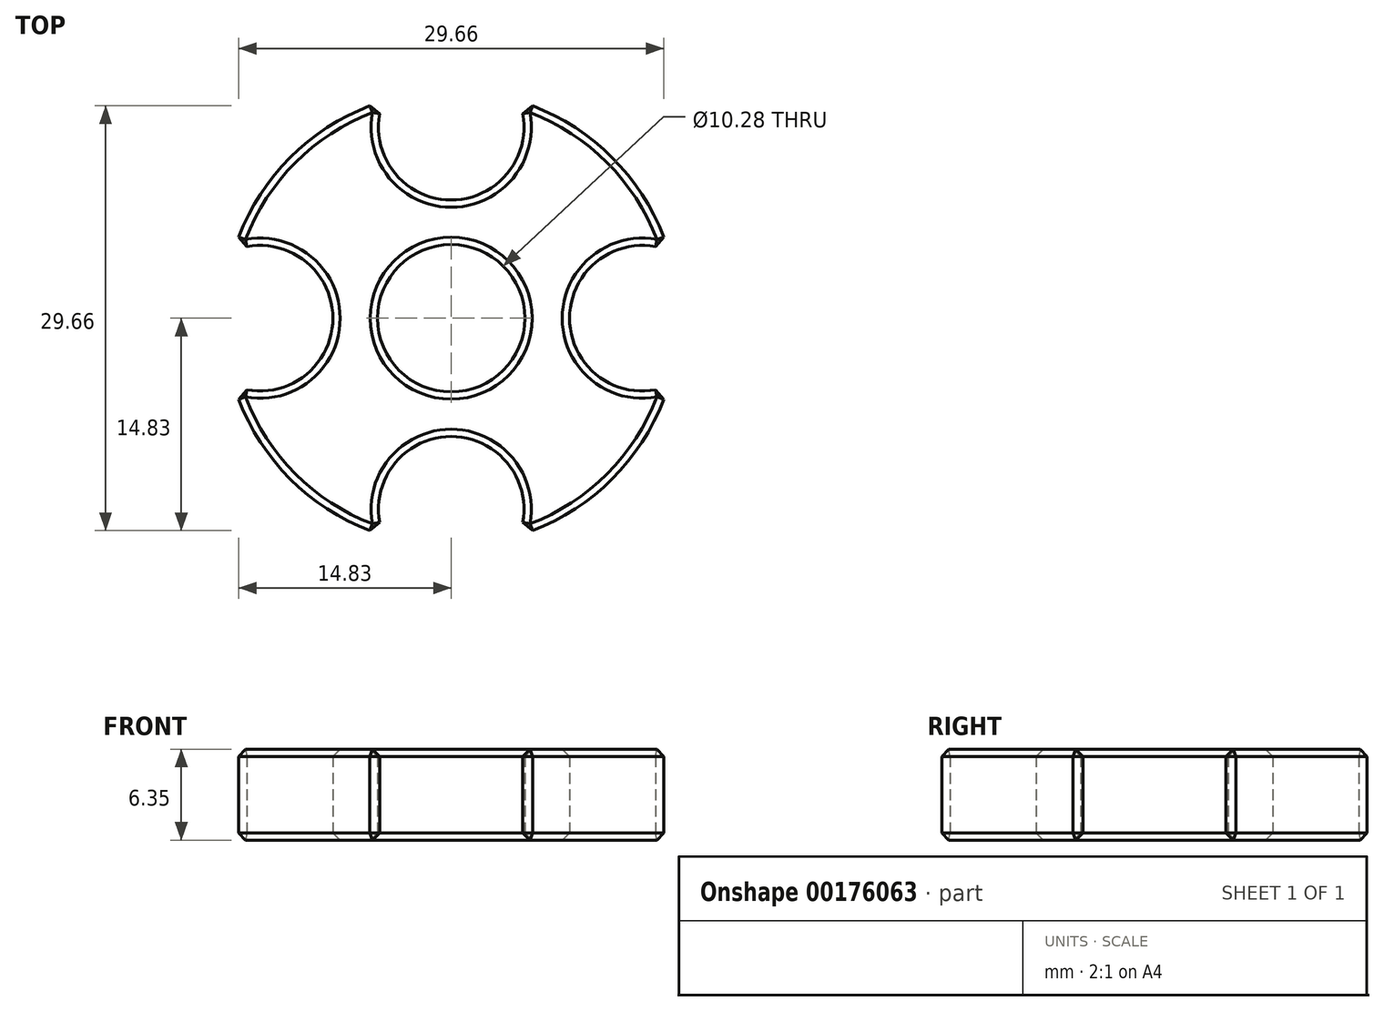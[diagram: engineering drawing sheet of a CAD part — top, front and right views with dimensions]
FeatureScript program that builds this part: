
annotation { "Feature Type Name" : "Feature", "Feature Type Description" : "" }
export const myFeature = defineFeature(function(context is Context, id is Id, definition is map)
    precondition{}
    {
        {
            var Q0;
            Q0=qCreatedBy(makeId("Top.planeOp"),FACE);
            var sketch = newSketch(context, id + "F0", { "sketchPlane" : qUnion([Q0])});
            skArc(sketch, "E0", {"start": v(-4.74, 15.15) * mm, "mid": v(-11.23, 11.23) * mm, "end": v(-15.15, 4.74) * mm});
            skCircle(sketch, "E1", {"center": v(0, 0) * mm, "radius": 5.14 * mm});
            skArc(sketch, "E2", {"start": v(-4.74, 15.15) * mm, "mid": v(0, 8.25) * mm, "end": v(4.74, 15.15) * mm});
            skArc(sketch, "E3.1.0", {"start": v(-15.15, -4.74) * mm, "mid": v(-8.25, 0) * mm, "end": v(-15.15, 4.74) * mm});
            skArc(sketch, "E3.2.0", {"start": v(4.74, -15.15) * mm, "mid": v(0, -8.25) * mm, "end": v(-4.74, -15.15) * mm});
            skArc(sketch, "E3.3.0", {"start": v(15.15, 4.74) * mm, "mid": v(8.25, 0) * mm, "end": v(15.15, -4.74) * mm});
            skArc(sketch, "E4.trimOffspring", {"start": v(-15.15, -4.74) * mm, "mid": v(-11.23, -11.23) * mm, "end": v(-4.74, -15.15) * mm});
            skArc(sketch, "E5.trimOffspring", {"start": v(4.74, -15.15) * mm, "mid": v(11.23, -11.23) * mm, "end": v(15.15, -4.74) * mm});
            skArc(sketch, "E6.trimOffspring", {"start": v(15.15, 4.74) * mm, "mid": v(11.23, 11.23) * mm, "end": v(4.74, 15.15) * mm});
            skSolve(sketch);
        }
        {
            var Q0;
            Q0=makeQuery(id+"F0.imprint","IMPRINT",FACE,{"disambiguationData":[TD([[makeQuery(id+"F0.imprint","IMPRINT",EDGE,{"derivedFrom":sQuery(id+"F0.wireOp",EDGE,"E0")}),1.0]])]});
            extrude(context, id + "F1", {"entities" : qUnion([Q0]), "depth" : 6.35 * mm});
        }
        {
            var Q0;
            Q0=makeQuery(id+"F1.opExtrude","CAP_FACE",FACE,{"disambiguationData":[OSD([sQuery(id+"F0.wireOp",EDGE,"E0"),sQuery(id+"F0.wireOp",EDGE,"E1"),sQuery(id+"F0.wireOp",EDGE,"E2"),sQuery(id+"F0.wireOp",EDGE,"E3.1.0"),sQuery(id+"F0.wireOp",EDGE,"E3.2.0"),sQuery(id+"F0.wireOp",EDGE,"E3.3.0"),sQuery(id+"F0.wireOp",EDGE,"E4.trimOffspring"),sQuery(id+"F0.wireOp",EDGE,"E5.trimOffspring"),sQuery(id+"F0.wireOp",EDGE,"E6.trimOffspring")])],"isStart":false});
            var Q1;
            Q1=makeQuery(id+"F1.opExtrude","CAP_FACE",FACE,{"disambiguationData":[OSD([sQuery(id+"F0.wireOp",EDGE,"E0"),sQuery(id+"F0.wireOp",EDGE,"E1"),sQuery(id+"F0.wireOp",EDGE,"E2"),sQuery(id+"F0.wireOp",EDGE,"E3.1.0"),sQuery(id+"F0.wireOp",EDGE,"E3.2.0"),sQuery(id+"F0.wireOp",EDGE,"E3.3.0"),sQuery(id+"F0.wireOp",EDGE,"E4.trimOffspring"),sQuery(id+"F0.wireOp",EDGE,"E5.trimOffspring"),sQuery(id+"F0.wireOp",EDGE,"E6.trimOffspring")])],"isStart":true});
            var Q2;
            Q2=makeQuery(id+"F1.opExtrude","SWEPT_EDGE",EDGE,{"disambiguationData":[OSD([sQuery(id+"F0.wireOp",EDGE,"E3.2.0"),sQuery(id+"F0.wireOp",EDGE,"E5.trimOffspring")])]});
            var Q3;
            Q3=makeQuery(id+"F1.opExtrude","SWEPT_EDGE",EDGE,{"disambiguationData":[OSD([sQuery(id+"F0.wireOp",EDGE,"E3.2.0"),sQuery(id+"F0.wireOp",EDGE,"E4.trimOffspring")])]});
            var Q4;
            Q4=makeQuery(id+"F1.opExtrude","SWEPT_EDGE",EDGE,{"disambiguationData":[OSD([sQuery(id+"F0.wireOp",EDGE,"E3.3.0"),sQuery(id+"F0.wireOp",EDGE,"E6.trimOffspring")])]});
            var Q5;
            Q5=makeQuery(id+"F1.opExtrude","SWEPT_EDGE",EDGE,{"disambiguationData":[OSD([sQuery(id+"F0.wireOp",EDGE,"E3.3.0"),sQuery(id+"F0.wireOp",EDGE,"E5.trimOffspring")])]});
            var Q6;
            Q6=makeQuery(id+"F1.opExtrude","SWEPT_EDGE",EDGE,{"disambiguationData":[OSD([sQuery(id+"F0.wireOp",EDGE,"E0"),sQuery(id+"F0.wireOp",EDGE,"E2")])]});
            var Q7;
            Q7=makeQuery(id+"F1.opExtrude","SWEPT_EDGE",EDGE,{"disambiguationData":[OSD([sQuery(id+"F0.wireOp",EDGE,"E0"),sQuery(id+"F0.wireOp",EDGE,"E3.1.0")])]});
            var Q8;
            Q8=makeQuery(id+"F1.opExtrude","SWEPT_EDGE",EDGE,{"disambiguationData":[OSD([sQuery(id+"F0.wireOp",EDGE,"E3.1.0"),sQuery(id+"F0.wireOp",EDGE,"E4.trimOffspring")])]});
            var Q9;
            Q9=makeQuery(id+"F1.opExtrude","SWEPT_EDGE",EDGE,{"disambiguationData":[OSD([sQuery(id+"F0.wireOp",EDGE,"E2"),sQuery(id+"F0.wireOp",EDGE,"E6.trimOffspring")])]});
            chamfer(context, id + "F2", {"entities" : qUnion([Q0, Q1, Q2, Q3, Q4, Q5, Q6, Q7, Q8, Q9]), "width" : 0.5 * mm, "tangentPropagation" : true});
        }
    });
